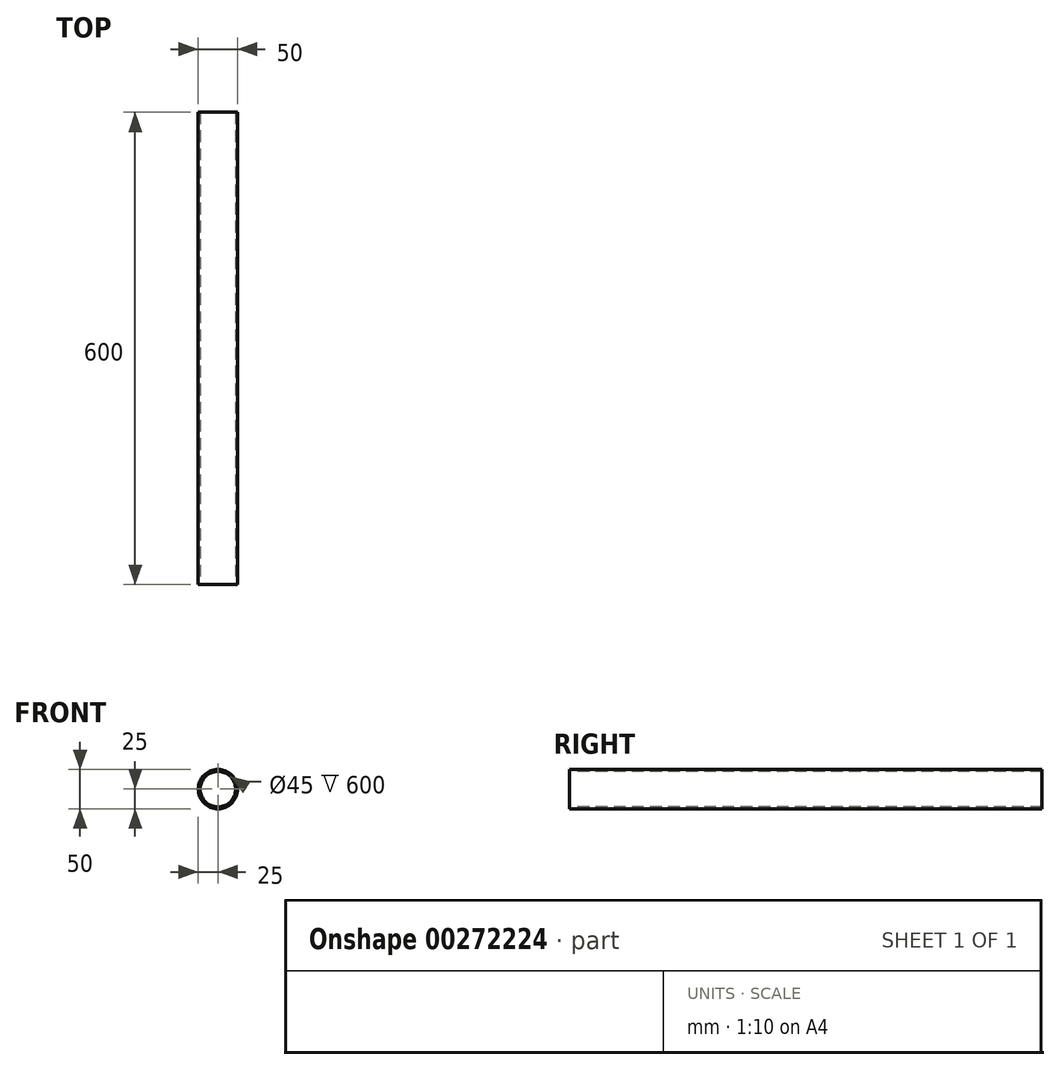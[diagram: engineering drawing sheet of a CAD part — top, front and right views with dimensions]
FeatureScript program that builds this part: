
annotation { "Feature Type Name" : "Feature", "Feature Type Description" : "" }
export const myFeature = defineFeature(function(context is Context, id is Id, definition is map)
    precondition{}
    {
        {
            var Q0;
            Q0=qCreatedBy(makeId("Front.planeOp"),FACE);
            var sketch = newSketch(context, id + "F0", { "sketchPlane" : qUnion([Q0])});
            skCircle(sketch, "E0", {"center": v(0, 0) * mm, "radius": 25 * mm});
            skSolve(sketch);
        }
        {
            var Q0;
            Q0=makeQuery(id+"F0.imprint","IMPRINT",FACE,{"disambiguationData":[TD([[makeQuery(id+"F0.imprint","IMPRINT",EDGE,{"derivedFrom":sQuery(id+"F0.wireOp",EDGE,"E0")}),1.0]])]});
            extrude(context, id + "F1", {"entities" : qUnion([Q0]), "oppositeDirection" : true, "depth" : 300 * mm});
        }
        {
            var Q0;
            Q0=makeQuery(id+"F1.opExtrude","SWEPT_BODY",BODY,{"disambiguationData":[OSD([sQuery(id+"F0.wireOp",EDGE,"E0")])]});
            var Q1;
            Q1=makeQuery(id+"F1.opExtrude","CAP_FACE",FACE,{"disambiguationData":[OSD([sQuery(id+"F0.wireOp",EDGE,"E0")])],"isStart":true});
            mirror(context, id + "F2", {"operationType" : NewBodyOperationType.ADD, "entities" : qUnion([Q0]), "mirrorPlane" : qUnion([Q1])});
        }
        {
            var Q0;
            Q0=makeQuery(id+"F2.opPattern","COPY",FACE,{"derivedFrom":makeQuery(id+"F1.opExtrude","CAP_FACE",FACE,{"disambiguationData":[OSD([sQuery(id+"F0.wireOp",EDGE,"E0")])],"isStart":false}),"instanceName":"1"});
            var sketch = newSketch(context, id + "F3", { "sketchPlane" : qUnion([Q0])});
            skCircle(sketch, "E1", {"center": v(0, 0) * mm, "radius": 22.5 * mm});
            skSolve(sketch);
        }
        {
            var Q0;
            Q0=makeQuery(id+"F3.imprint","IMPRINT",FACE,{"disambiguationData":[TD([[makeQuery(id+"F3.imprint","IMPRINT",EDGE,{"derivedFrom":sQuery(id+"F3.wireOp",EDGE,"E1")}),1.0]])]});
            extrude(context, id + "F4", {"entities" : qUnion([Q0]), "operationType" : NewBodyOperationType.REMOVE, "oppositeDirection" : true, "depth" : 600 * mm});
        }
    });
